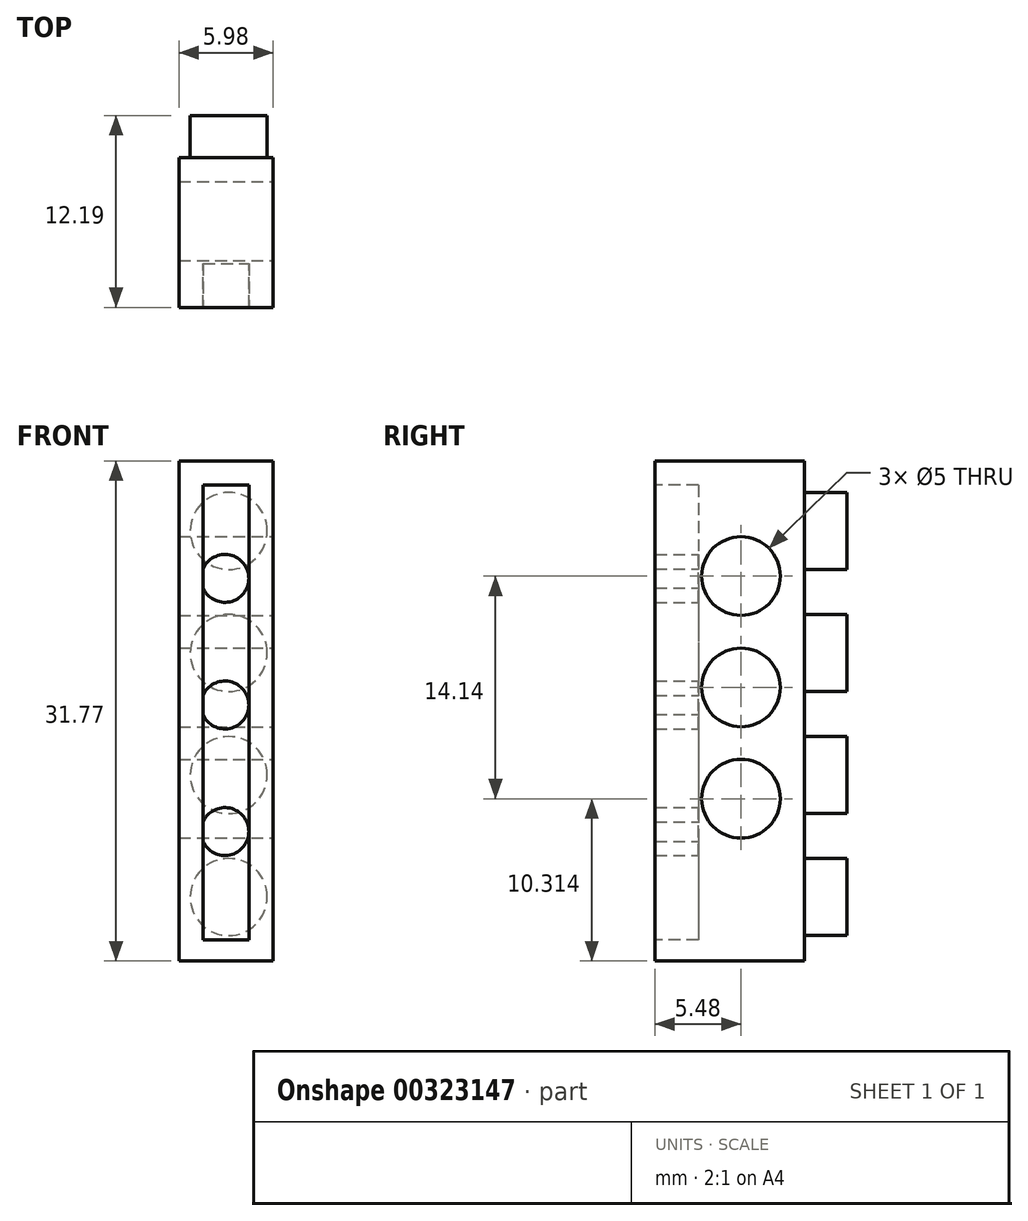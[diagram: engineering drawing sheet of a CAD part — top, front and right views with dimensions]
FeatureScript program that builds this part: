
annotation { "Feature Type Name" : "Feature", "Feature Type Description" : "" }
export const myFeature = defineFeature(function(context is Context, id is Id, definition is map)
    precondition{}
    {
        {
            var Q0;
            Q0=qCreatedBy(makeId("Front.planeOp"),FACE);
            var sketch = newSketch(context, id + "F0", { "sketchPlane" : qUnion([Q0])});
            skLineSegment(sketch, "E0.bottom", {"start": v(-24.58, 26.53) * mm, "end": v(-18.6, 26.53) * mm});
            skLineSegment(sketch, "E0.top", {"start": v(-24.58, -5.24) * mm, "end": v(-18.6, -5.24) * mm});
            skLineSegment(sketch, "E0.left", {"start": v(-24.58, 26.53) * mm, "end": v(-24.58, -5.24) * mm});
            skLineSegment(sketch, "E0.right", {"start": v(-18.6, 26.53) * mm, "end": v(-18.6, -5.24) * mm});
            skSolve(sketch);
        }
        {
            var Q0;
            Q0=makeQuery(id+"F0.imprint","IMPRINT",FACE,{"disambiguationData":[TD([[makeQuery(id+"F0.imprint","IMPRINT",EDGE,{"derivedFrom":sQuery(id+"F0.wireOp",EDGE,"E0.bottom")}),-1.0]])]});
            extrude(context, id + "F1", {"entities" : qUnion([Q0]), "depth" : 9.5 * mm});
        }
        {
            var Q0;
            Q0=qCreatedBy(makeId("Right.planeOp"),FACE);
            var sketch = newSketch(context, id + "F2", { "sketchPlane" : qUnion([Q0])});
            skCircle(sketch, "E1", {"center": v(-4.02, 19.21) * mm, "radius": 2.45 * mm});
            skCircle(sketch, "E2", {"center": v(-4.02, 12.14) * mm, "radius": 2.45 * mm});
            skCircle(sketch, "E3", {"center": v(-4.02, 5.07) * mm, "radius": 2.45 * mm});
            skSolve(sketch);
        }
        {
            var Q0;
            Q0=sQuery(id+"F2.wireOp",VERTEX,"E1.center");
            var Q1;
            Q1=sQuery(id+"F2.wireOp",VERTEX,"E2.center");
            var Q2;
            Q2=sQuery(id+"F2.wireOp",VERTEX,"E3.center");
            var Q3;
            Q3=makeQuery(id+"F1.opExtrude","SWEPT_BODY",BODY,{"disambiguationData":[OSD([sQuery(id+"F0.wireOp",EDGE,"E0.bottom"),sQuery(id+"F0.wireOp",EDGE,"E0.top"),sQuery(id+"F0.wireOp",EDGE,"E0.left"),sQuery(id+"F0.wireOp",EDGE,"E0.right")])]});
            hole(context, id + "F3", {"style" : HoleStyle.SIMPLE, "endStyle" : HoleEndStyle.THROUGH, "holeDiameter" : 5 * mm, "tappedDepth" : 12 * mm, "tapClearance" : 3, "locations" : qUnion([Q0, Q1, Q2]), "scope" : qUnion([Q3])});
        }
        {
            var Q0;
            Q0=qCreatedBy(makeId("Front.planeOp"),FACE);
            var sketch = newSketch(context, id + "F4", { "sketchPlane" : qUnion([Q0])});
            skCircle(sketch, "E4", {"center": v(-21.42, 22.08) * mm, "radius": 2.44 * mm});
            skCircle(sketch, "E5", {"center": v(-21.42, 14.33) * mm, "radius": 2.44 * mm});
            skCircle(sketch, "E6", {"center": v(-21.42, 6.58) * mm, "radius": 2.44 * mm});
            skCircle(sketch, "E7", {"center": v(-21.42, -1.17) * mm, "radius": 2.44 * mm});
            skSolve(sketch);
        }
        {
            var Q0;
            Q0=makeQuery(id+"F4.imprint","IMPRINT",FACE,{"disambiguationData":[TD([[makeQuery(id+"F4.imprint","IMPRINT",EDGE,{"derivedFrom":sQuery(id+"F4.wireOp",EDGE,"E4")}),1.0]])]});
            var Q1;
            Q1=makeQuery(id+"F4.imprint","IMPRINT",FACE,{"disambiguationData":[TD([[makeQuery(id+"F4.imprint","IMPRINT",EDGE,{"derivedFrom":sQuery(id+"F4.wireOp",EDGE,"E5")}),1.0]])]});
            var Q2;
            Q2=makeQuery(id+"F4.imprint","IMPRINT",FACE,{"disambiguationData":[TD([[makeQuery(id+"F4.imprint","IMPRINT",EDGE,{"derivedFrom":sQuery(id+"F4.wireOp",EDGE,"E6")}),1.0]])]});
            var Q3;
            Q3=makeQuery(id+"F4.imprint","IMPRINT",FACE,{"disambiguationData":[TD([[makeQuery(id+"F4.imprint","IMPRINT",EDGE,{"derivedFrom":sQuery(id+"F4.wireOp",EDGE,"E7")}),1.0]])]});
            extrude(context, id + "F5", {"entities" : qUnion([Q0, Q1, Q2, Q3]), "operationType" : NewBodyOperationType.ADD, "oppositeDirection" : true, "depth" : 2.69 * mm});
        }
        {
            var Q0;
            Q0=makeQuery(id+"F1.opExtrude","CAP_FACE",FACE,{"disambiguationData":[OSD([sQuery(id+"F0.wireOp",EDGE,"E0.bottom"),sQuery(id+"F0.wireOp",EDGE,"E0.top"),sQuery(id+"F0.wireOp",EDGE,"E0.left"),sQuery(id+"F0.wireOp",EDGE,"E0.right")])],"isStart":false});
            var sketch = newSketch(context, id + "F6", { "sketchPlane" : qUnion([Q0])});
            skLineSegment(sketch, "E8.bottom", {"start": v(-23.05, 25) * mm, "end": v(-20.13, 25) * mm});
            skLineSegment(sketch, "E8.top", {"start": v(-23.05, -3.9) * mm, "end": v(-20.13, -3.9) * mm});
            skLineSegment(sketch, "E8.left", {"start": v(-23.05, 25) * mm, "end": v(-23.05, -3.9) * mm});
            skLineSegment(sketch, "E8.right", {"start": v(-20.13, 25) * mm, "end": v(-20.13, -3.9) * mm});
            skSolve(sketch);
        }
        {
            var Q0;
            Q0=makeQuery(id+"F6.imprint","IMPRINT",FACE,{"disambiguationData":[TD([[makeQuery(id+"F6.imprint","IMPRINT",EDGE,{"derivedFrom":sQuery(id+"F6.wireOp",EDGE,"E8.bottom")}),-1.0]])]});
            extrude(context, id + "F7", {"entities" : qUnion([Q0]), "operationType" : NewBodyOperationType.REMOVE, "oppositeDirection" : true, "depth" : 2.78 * mm});
        }
        {
            var Q0;
            Q0=makeQuery(id+"F7.boolean.opBoolean","COPY",FACE,{"derivedFrom":makeQuery(id+"F7.opExtrude","CAP_FACE",FACE,{"disambiguationData":[OSD([sQuery(id+"F6.wireOp",EDGE,"E8.bottom"),sQuery(id+"F6.wireOp",EDGE,"E8.top"),sQuery(id+"F6.wireOp",EDGE,"E8.left"),sQuery(id+"F6.wireOp",EDGE,"E8.right")])],"isStart":false})});
            var sketch = newSketch(context, id + "F8", { "sketchPlane" : qUnion([Q0])});
            skCircle(sketch, "E9", {"center": v(-21.66, 19.07) * mm, "radius": 1.52 * mm});
            skCircle(sketch, "E10", {"center": v(-21.66, 11.03) * mm, "radius": 1.52 * mm});
            skCircle(sketch, "E11", {"center": v(-21.66, 2.99) * mm, "radius": 1.52 * mm});
            skSolve(sketch);
        }
        {
            var Q0;
            {var subQ0=sQuery(id+"F8.wireOp",EDGE,"E9");var subQ1=makeQuery(id+"F7.boolean.opBoolean","COPY",EDGE,{"derivedFrom":makeQuery(id+"F7.opExtrude","CAP_EDGE",EDGE,{"disambiguationData":[OSD([sQuery(id+"F6.wireOp",EDGE,"E8.left")])],"isStart":false})});var subQ2=makeQuery(id+"F8.imprint","INTERSECT",VERTEX,{"disambiguationData":[OD(0.0)],"derivedFrom":[subQ1,subQ0]});Q0=makeQuery(id+"F8.imprint","IMPRINT",FACE,{"disambiguationData":[TD([[makeQuery(id+"F8.imprint","IMPRINT",EDGE,{"disambiguationData":[TD([[subQ2,1.0]])],"derivedFrom":subQ0}),1.0]])]});}
            var Q1;
            {var subQ0=sQuery(id+"F8.wireOp",EDGE,"E10");var subQ1=makeQuery(id+"F7.boolean.opBoolean","COPY",EDGE,{"derivedFrom":makeQuery(id+"F7.opExtrude","CAP_EDGE",EDGE,{"disambiguationData":[OSD([sQuery(id+"F6.wireOp",EDGE,"E8.left")])],"isStart":false})});var subQ2=makeQuery(id+"F8.imprint","INTERSECT",VERTEX,{"disambiguationData":[OD(0.0)],"derivedFrom":[subQ1,subQ0]});Q1=makeQuery(id+"F8.imprint","IMPRINT",FACE,{"disambiguationData":[TD([[makeQuery(id+"F8.imprint","IMPRINT",EDGE,{"disambiguationData":[TD([[subQ2,1.0]])],"derivedFrom":subQ0}),1.0]])]});}
            var Q2;
            {var subQ0=sQuery(id+"F8.wireOp",EDGE,"E11");var subQ1=makeQuery(id+"F7.boolean.opBoolean","COPY",EDGE,{"derivedFrom":makeQuery(id+"F7.opExtrude","CAP_EDGE",EDGE,{"disambiguationData":[OSD([sQuery(id+"F6.wireOp",EDGE,"E8.left")])],"isStart":false})});var subQ2=makeQuery(id+"F8.imprint","INTERSECT",VERTEX,{"disambiguationData":[OD(0.0)],"derivedFrom":[subQ1,subQ0]});Q2=makeQuery(id+"F8.imprint","IMPRINT",FACE,{"disambiguationData":[TD([[makeQuery(id+"F8.imprint","IMPRINT",EDGE,{"disambiguationData":[TD([[subQ2,-1.0]])],"derivedFrom":subQ0}),1.0]])]});}
            extrude(context, id + "F9", {"entities" : qUnion([Q0, Q1, Q2]), "operationType" : NewBodyOperationType.ADD, "depth" : 2.75 * mm});
        }
    });
